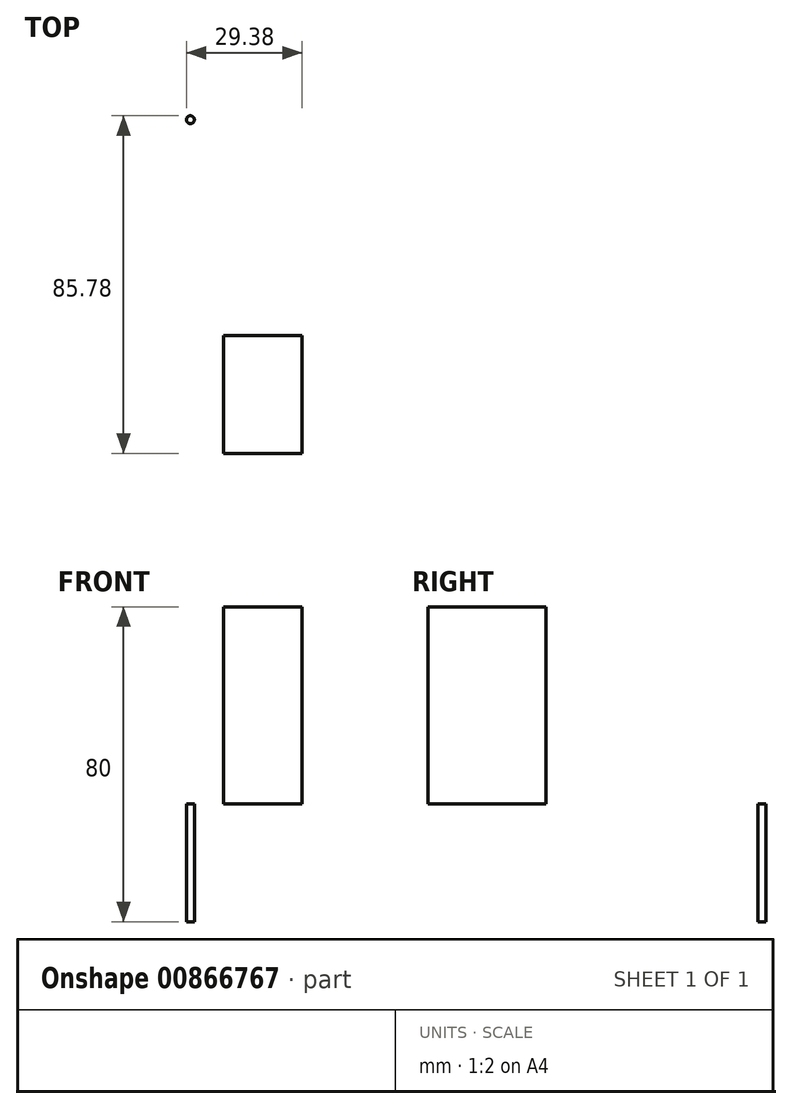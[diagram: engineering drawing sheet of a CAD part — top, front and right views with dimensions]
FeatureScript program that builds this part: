
annotation { "Feature Type Name" : "Feature", "Feature Type Description" : "" }
export const myFeature = defineFeature(function(context is Context, id is Id, definition is map)
    precondition{}
    {
        {
            var Q0;
            Q0=qCreatedBy(makeId("Top.planeOp"),FACE);
            var sketch = newSketch(context, id + "F0", { "sketchPlane" : qUnion([Q0])});
            skCircle(sketch, "E0", {"center": v(-18.38, 9.3) * mm, "radius": 1 * mm});
            skSolve(sketch);
        }
        {
            var Q0;
            Q0=makeQuery(id+"F0.imprint","IMPRINT",FACE,{"disambiguationData":[TD([[makeQuery(id+"F0.imprint","IMPRINT",EDGE,{"derivedFrom":sQuery(id+"F0.wireOp",EDGE,"E0")}),1.0]])]});
            extrude(context, id + "F1", {"entities" : qUnion([Q0]), "oppositeDirection" : true, "depth" : 30 * mm, "offsetDistance" : 25 * mm});
        }
        {
            var Q0;
            Q0=qCreatedBy(makeId("Right.planeOp"),FACE);
            var sketch = newSketch(context, id + "F2", { "sketchPlane" : qUnion([Q0])});
            skLineSegment(sketch, "E1.bottom", {"start": v(-45.48, 0) * mm, "end": v(-75.48, 0) * mm});
            skLineSegment(sketch, "E1.top", {"start": v(-45.48, 50) * mm, "end": v(-75.48, 50) * mm});
            skLineSegment(sketch, "E1.left", {"start": v(-45.48, 0) * mm, "end": v(-45.48, 50) * mm});
            skLineSegment(sketch, "E1.right", {"start": v(-75.48, 0) * mm, "end": v(-75.48, 50) * mm});
            skPoint(sketch, "E1.middle", {"position": v(-60.48, 25) * mm});
            skSolve(sketch);
        }
        {
            var Q0;
            Q0=makeQuery(id+"F2.imprint","IMPRINT",FACE,{"disambiguationData":[TD([[makeQuery(id+"F2.imprint","IMPRINT",EDGE,{"derivedFrom":sQuery(id+"F2.wireOp",EDGE,"E1.bottom")}),-1.0]])]});
            extrude(context, id + "F3", {"entities" : qUnion([Q0]), "endBound" : BoundingType.SYMMETRIC, "depth" : 20 * mm, "offsetDistance" : 25 * mm});
        }
    });
